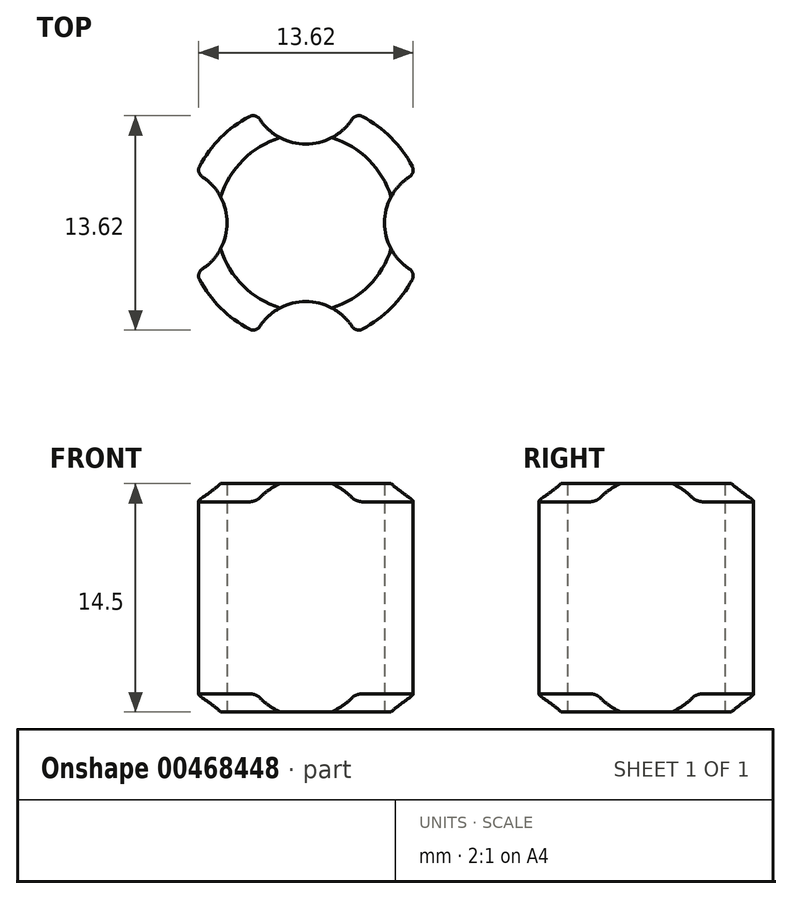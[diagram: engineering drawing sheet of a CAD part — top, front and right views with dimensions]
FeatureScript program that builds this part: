
annotation { "Feature Type Name" : "Feature", "Feature Type Description" : "" }
export const myFeature = defineFeature(function(context is Context, id is Id, definition is map)
    precondition{}
    {
        {
            var Q0;
            Q0=qCreatedBy(makeId("Top.planeOp"),FACE);
            var sketch = newSketch(context, id + "F0", { "sketchPlane" : qUnion([Q0])});
            skArc(sketch, "E0", {"start": v(-6.97, -3.15) * mm, "mid": v(-5.4, -5.4) * mm, "end": v(-3.15, -6.97) * mm});
            skArc(sketch, "E1", {"start": v(-3.15, 6.97) * mm, "mid": v(0, 5) * mm, "end": v(3.15, 6.97) * mm});
            skArc(sketch, "E2", {"start": v(3.15, -6.97) * mm, "mid": v(0, -5) * mm, "end": v(-3.15, -6.97) * mm});
            skArc(sketch, "E3", {"start": v(-6.97, -3.15) * mm, "mid": v(-5, 0) * mm, "end": v(-6.97, 3.15) * mm});
            skArc(sketch, "E4", {"start": v(6.97, 3.15) * mm, "mid": v(5, 0) * mm, "end": v(6.97, -3.15) * mm});
            skArc(sketch, "E5.trimOffspring", {"start": v(-3.15, 6.97) * mm, "mid": v(-5.4, 5.4) * mm, "end": v(-6.97, 3.15) * mm});
            skArc(sketch, "E6.trimOffspring", {"start": v(6.97, 3.15) * mm, "mid": v(5.4, 5.4) * mm, "end": v(3.15, 6.97) * mm});
            skArc(sketch, "E7.trimOffspring", {"start": v(3.15, -6.97) * mm, "mid": v(5.4, -5.4) * mm, "end": v(6.97, -3.15) * mm});
            skSolve(sketch);
        }
        {
            var Q0;
            Q0 = qSketchRegion(id + "F0", true);
            extrude(context, id + "F1", {"entities" : qUnion([Q0]), "endBound" : BoundingType.SYMMETRIC, "depth" : 14.5 * mm, "offsetDistance" : 25 * mm});
        }
        {
            var Q0;
            Q0=makeQuery(id+"F1.opExtrude","SWEPT_EDGE",EDGE,{"disambiguationData":[OSD([sQuery(id+"F0.wireOp",EDGE,"E1"),sQuery(id+"F0.wireOp",EDGE,"E5.trimOffspring")])]});
            var Q1;
            Q1=makeQuery(id+"F1.opExtrude","SWEPT_EDGE",EDGE,{"disambiguationData":[OSD([sQuery(id+"F0.wireOp",EDGE,"E3"),sQuery(id+"F0.wireOp",EDGE,"E5.trimOffspring")])]});
            var Q2;
            Q2=makeQuery(id+"F1.opExtrude","SWEPT_EDGE",EDGE,{"disambiguationData":[OSD([sQuery(id+"F0.wireOp",EDGE,"E0"),sQuery(id+"F0.wireOp",EDGE,"E3")])]});
            var Q3;
            Q3=makeQuery(id+"F1.opExtrude","SWEPT_EDGE",EDGE,{"disambiguationData":[OSD([sQuery(id+"F0.wireOp",EDGE,"E0"),sQuery(id+"F0.wireOp",EDGE,"E2")])]});
            var Q4;
            Q4=makeQuery(id+"F1.opExtrude","SWEPT_EDGE",EDGE,{"disambiguationData":[OSD([sQuery(id+"F0.wireOp",EDGE,"E2"),sQuery(id+"F0.wireOp",EDGE,"E7.trimOffspring")])]});
            var Q5;
            Q5=makeQuery(id+"F1.opExtrude","SWEPT_EDGE",EDGE,{"disambiguationData":[OSD([sQuery(id+"F0.wireOp",EDGE,"E4"),sQuery(id+"F0.wireOp",EDGE,"E7.trimOffspring")])]});
            var Q6;
            Q6=makeQuery(id+"F1.opExtrude","SWEPT_EDGE",EDGE,{"disambiguationData":[OSD([sQuery(id+"F0.wireOp",EDGE,"E4"),sQuery(id+"F0.wireOp",EDGE,"E6.trimOffspring")])]});
            var Q7;
            Q7=makeQuery(id+"F1.opExtrude","SWEPT_EDGE",EDGE,{"disambiguationData":[OSD([sQuery(id+"F0.wireOp",EDGE,"E1"),sQuery(id+"F0.wireOp",EDGE,"E6.trimOffspring")])]});
            fillet(context, id + "F2", {"entities" : qUnion([Q0, Q1, Q2, Q3, Q4, Q5, Q6, Q7]), "tangentPropagation" : true, "radius" : .5 * mm, "defaultsChanged" : true, "vertexSettings" : [], "allowEdgeOverflow" : false});
        }
        {
            var Q0;
            Q0=qCreatedBy(makeId("Right.planeOp"),FACE);
            var sketch = newSketch(context, id + "F3", { "sketchPlane" : qUnion([Q0])});
            skLineSegment(sketch, "E8", {"start": v(-5.65, 7.25) * mm, "end": v(-7.65, 7.25) * mm});
            skLineSegment(sketch, "E9", {"start": v(-7.65, 7.25) * mm, "end": v(-7.65, 6.1) * mm});
            skLineSegment(sketch, "E10", {"start": v(-7.65, 6.1) * mm, "end": v(-5.65, 7.25) * mm});
            skLineSegment(sketch, "E11", {"start": v(0, 7.24) * mm, "end": v(0, -7.23) * mm, "construction": true});
            skLineSegment(sketch, "E12", {"start": v(-7.65, -6.1) * mm, "end": v(-7.65, -7.25) * mm});
            skLineSegment(sketch, "E13", {"start": v(-7.65, -7.25) * mm, "end": v(-5.65, -7.25) * mm});
            skLineSegment(sketch, "E14", {"start": v(-5.65, -7.25) * mm, "end": v(-7.65, -6.1) * mm});
            skSolve(sketch);
        }
        {
            var Q0;
            Q0=makeQuery(id+"F3.imprint","IMPRINT",FACE,{"disambiguationData":[TD([[makeQuery(id+"F3.imprint","IMPRINT",EDGE,{"derivedFrom":sQuery(id+"F3.wireOp",EDGE,"E8")}),1.0]])]});
            var Q1;
            Q1=makeQuery(id+"F3.imprint","IMPRINT",FACE,{"disambiguationData":[TD([[makeQuery(id+"F3.imprint","IMPRINT",EDGE,{"derivedFrom":sQuery(id+"F3.wireOp",EDGE,"E12")}),1.0]])]});
            var Q2;
            Q2=sQuery(id+"F3.wireOp",EDGE,"E11");
            var Q3;
            Q3=sQuery(id+"F3.wireOp",EDGE,"E11");
            revolve(context, id + "F4", {"operationType" : NewBodyOperationType.REMOVE, "surfaceOperationType" : NewSurfaceOperationType.NEW, "entities" : qUnion([Q0, Q1]), "surfaceEntities" : qUnion([Q2]), "axis" : qUnion([Q3]), "revolveType" : RevolveType.FULL, "oppositeDirection" : true});
        }
    });
